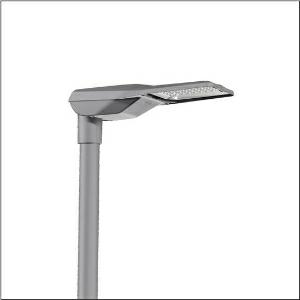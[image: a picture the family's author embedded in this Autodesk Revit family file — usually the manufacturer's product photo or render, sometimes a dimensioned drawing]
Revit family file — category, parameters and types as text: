
# Revit family: streetlight_sl_21_iq_mini___stw1_0a_5xe2e31d08jb_eadb
name_source: partatom
category: Lighting Fixtures
units: mm (PartAtom-declared; Revit-internal decimal feet)

## family parameters
Cut with Voids When Loaded = No
Host = Face
Light Source = No
Part Type = Normal
Room Calculation Point = No
Round Connector Dimension = Use Diameter
Shared = No

## types (1)
- --- (1 x LED, 10820 lm, 71.6 W, 3000K)
    Apparent Load = 72 VA
    CIE Flux Codes = 39 75 98 100 100
    Color Rendering = 70
    Color Temperature = 3000K
    Default Elevation = 1800 mm
    Description = Streetlight SL 21 iQ mini, mast luminaire, primary light control with lens, of PMMA, primary optical cover: cover, of toughened safety glass, transparent, light distribution: STW1.0a, light emission: direct distribution, primary light characteristic: asymmetric, installation type: post-top, side-entry, LED, High Power LED, rated luminous flux: 10.820lm, luminous efficacy: 151lm/W, light colour: 730, colour temperature: 3000K, control gear: iQ-Comfort, control: Auto-Match, Temp-Guard, Lumen-Switch, Night-Set, Smart-Wire, Light-Fading, Desk-Remote (wireless, voltage-free reading and setting of iQ features in the workshop via application-optimized NFC function/RFID function), optimised constant luminous flux control (CLO 2.0), pre-setting: linear dimming characteristic, mains connection: 220..240V, AC, 50/60Hz, start of lifetime: 72W, end of service life: 75W, reduction: 33W, luminaire housing, of diecast aluminium, powder-coated, SITECO metallic grey (DB 702S), corrosivity category C5 high according to DIN EN ISO 12944, please order mast flange separately, inclination adjustable: 0°, 5°, 10°, 15°, sealing non-destructively replaceable, multi-level sealing system, length: 628mm, width: 235mm, height: 110mm, mast flange for spigot size: 42mm (side-entry): 5XC10008XM4, 60/48mm (side-entry/post-top): 5XC10108XM2, 76/60mm (side-entry/post-top): 5XC10108XM1, mounting height: 4..8m, protection rating (complete): IP66, insulation class (complete): insulation class II (safety insulation), certification: CE, ENEC, ENEC+, VDE, impact resistance: IK10, permissible operating ambient temperature for outdoor applications: -40..+50°C, standard-compliant lighting for roads and squares, packaging unit: 1 piece

Light Distribution: STW1.0a
    Height = 110 mm
    Lamp = 1 x LED
    Lamp Light Flux = 10820 lm
    Lamp Power = 71.6 W
    Lamp count = 1
    Length = 625 mm
    Luminous efficacy = 151 lm/W
    Manufacturer = Siteco
    ModVariant = No
    Model = 5XE2E31D08JB
    Number of Poles = 1
    OnlyDefault = Yes
    Power Factor = 1
    Product Name = Streetlight SL 21 iQ mini | STW1.0a
    Product group = mast luminaire | pylon top
    ProductGroupID = 6100
    Protection Class = Protection class II
    Protection Degree = IP 66
    RLX_Detail_Level = 1
    RLX_Emergency_Light_Flux = 0 lm
    RLX_Emergency_Type = 0
    RLX_Emergency_Type_DB = No
    RlxData = <blob elided: 26401 chars, md5=7bc96fb4>
    Socket = socket
    Standby Power = 0 W
    System Light Flux = 10820 lm
    System Power = 72 W
    Type Comments = factory setting: luminous flux: 100 % | dim-lin: 254 | 746 mA
    Type Image = l_1003519.jpg
    URL = http://relux.com
    VarID = @adj_169711
    Voltage = 0 V
    Weight = 0.00 kg
    Width = 234 mm

## geometry (parser evidence)
native form markers: Blend x4, Sweep x11
no freeform markers — native parametric forms only
